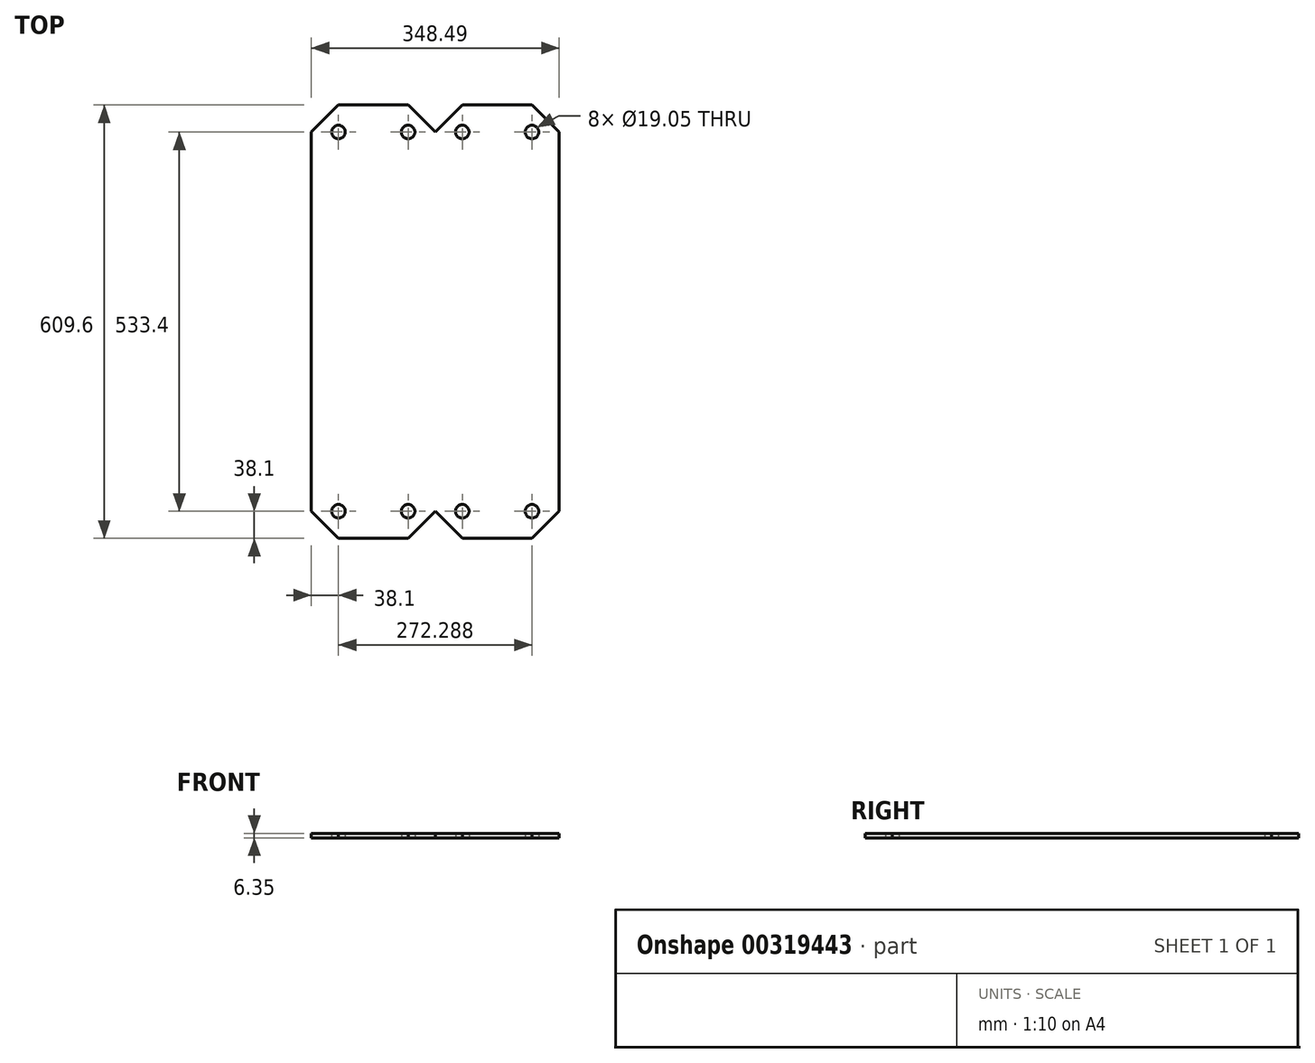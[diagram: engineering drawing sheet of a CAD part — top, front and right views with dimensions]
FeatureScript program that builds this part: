
annotation { "Feature Type Name" : "Feature", "Feature Type Description" : "" }
export const myFeature = defineFeature(function(context is Context, id is Id, definition is map)
    precondition{}
    {
        {
            var Q0;
            Q0=qCreatedBy(makeId("Top.planeOp"),FACE);
            var sketch = newSketch(context, id + "F0", { "sketchPlane" : qUnion([Q0])});
            skLineSegment(sketch, "E0.top", {"start": v(348.49, 0) * mm, "end": v(212.34, 0) * mm});
            skLineSegment(sketch, "E0.left", {"start": v(348.49, 609.6) * mm, "end": v(348.49, 0) * mm});
            skLineSegment(sketch, "E0.right", {"start": v(0, 609.6) * mm, "end": v(0, 0) * mm});
            skPoint(sketch, "E1.orphan", {"position": v(348.49, 609.6) * mm});
            skLineSegment(sketch, "E2", {"start": v(174.24, 609.6) * mm, "end": v(174.24, 0) * mm, "construction": true});
            skLineSegment(sketch, "E3", {"start": v(136.14, 609.6) * mm, "end": v(174.24, 571.5) * mm});
            skLineSegment(sketch, "E4", {"start": v(174.24, 571.5) * mm, "end": v(212.34, 609.6) * mm});
            skLineSegment(sketch, "E5", {"start": v(136.14, 0) * mm, "end": v(174.24, 38.1) * mm});
            skLineSegment(sketch, "E6", {"start": v(174.24, 38.1) * mm, "end": v(212.34, 0) * mm});
            skLineSegment(sketch, "E7.trimOffspring", {"start": v(136.14, 609.6) * mm, "end": v(0, 609.6) * mm});
            skLineSegment(sketch, "E8.trimOffspring", {"start": v(136.14, 0) * mm, "end": v(0, 0) * mm});
            skLineSegment(sketch, "E9", {"start": v(212.34, 609.6) * mm, "end": v(348.49, 609.6) * mm});
            skSolve(sketch);
        }
        {
            var Q0;
            Q0 = qSketchRegion(id + "F0", true);
            extrude(context, id + "F1", {"entities" : qUnion([Q0]), "depth" : 6.35 * mm});
        }
        {
            var Q0;
            Q0=makeQuery(id+"F1.opExtrude","SWEPT_EDGE",EDGE,{"disambiguationData":[OSD([sQuery(id+"F0.wireOp",EDGE,"E0.right"),sQuery(id+"F0.wireOp",EDGE,"E7.trimOffspring")])]});
            var Q1;
            Q1=makeQuery(id+"F1.opExtrude","SWEPT_EDGE",EDGE,{"disambiguationData":[OSD([sQuery(id+"F0.wireOp",EDGE,"E0.left"),sQuery(id+"F0.wireOp",EDGE,"E9")])]});
            var Q2;
            Q2=makeQuery(id+"F1.opExtrude","SWEPT_EDGE",EDGE,{"disambiguationData":[OSD([sQuery(id+"F0.wireOp",EDGE,"E0.top"),sQuery(id+"F0.wireOp",EDGE,"E0.left")])]});
            var Q3;
            Q3=makeQuery(id+"F1.opExtrude","SWEPT_EDGE",EDGE,{"disambiguationData":[OSD([sQuery(id+"F0.wireOp",EDGE,"E0.right"),sQuery(id+"F0.wireOp",EDGE,"E8.trimOffspring")])]});
            chamfer(context, id + "F2", {"entities" : qUnion([Q0, Q1, Q2, Q3]), "width" : 38.1 * mm, "tangentPropagation" : true});
        }
        {
            var Q0;
            Q0=makeQuery(id+"F1.opExtrude","CAP_FACE",FACE,{"disambiguationData":[OSD([sQuery(id+"F0.wireOp",EDGE,"E0.top"),sQuery(id+"F0.wireOp",EDGE,"E0.left"),sQuery(id+"F0.wireOp",EDGE,"E0.right"),sQuery(id+"F0.wireOp",EDGE,"E3"),sQuery(id+"F0.wireOp",EDGE,"E4"),sQuery(id+"F0.wireOp",EDGE,"E5"),sQuery(id+"F0.wireOp",EDGE,"E6"),sQuery(id+"F0.wireOp",EDGE,"E7.trimOffspring"),sQuery(id+"F0.wireOp",EDGE,"E8.trimOffspring"),sQuery(id+"F0.wireOp",EDGE,"E9")])],"isStart":true});
            var sketch = newSketch(context, id + "F3", { "sketchPlane" : qUnion([Q0])});
            skCircle(sketch, "E10", {"center": v(38.1, -571.5) * mm, "radius": 9.53 * mm});
            skCircle(sketch, "E11", {"center": v(136.14, -571.5) * mm, "radius": 9.53 * mm});
            skCircle(sketch, "E12", {"center": v(212.34, -571.5) * mm, "radius": 9.53 * mm});
            skCircle(sketch, "E13", {"center": v(310.39, -571.5) * mm, "radius": 9.52 * mm});
            skLineSegment(sketch, "E14", {"start": v(0, -304.8) * mm, "end": v(348.49, -304.8) * mm, "construction": true});
            skCircle(sketch, "E15.MirrorC", {"center": v(38.1, -38.1) * mm, "radius": 9.53 * mm});
            skCircle(sketch, "E16.MirrorC", {"center": v(136.14, -38.1) * mm, "radius": 9.53 * mm});
            skCircle(sketch, "E17.MirrorC", {"center": v(212.34, -38.1) * mm, "radius": 9.53 * mm});
            skCircle(sketch, "E18.MirrorC", {"center": v(310.39, -38.1) * mm, "radius": 9.52 * mm});
            skSolve(sketch);
        }
        {
            var Q0;
            Q0 = qSketchRegion(id + "F3", true);
            extrude(context, id + "F4", {"entities" : qUnion([Q0]), "operationType" : NewBodyOperationType.REMOVE, "endBound" : BoundingType.THROUGH_ALL, "oppositeDirection" : true, "depth" : 25.4 * mm});
        }
    });
